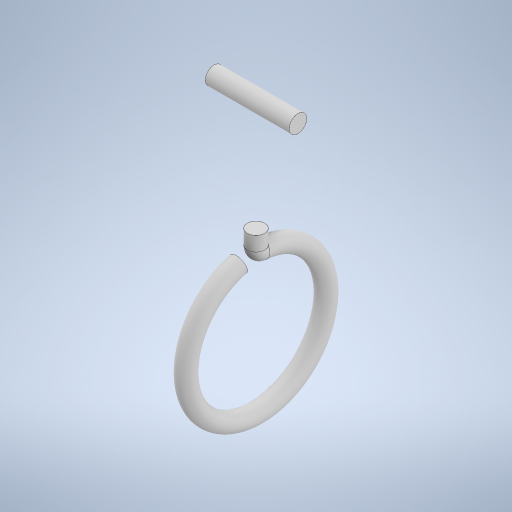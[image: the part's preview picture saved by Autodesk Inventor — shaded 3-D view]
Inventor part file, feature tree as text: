
AUTODESK INVENTOR PART (.ipt)
format: ipt  version: 2023 (Build 270158000, 158)  size: 293,376 bytes
history: native  units: in
note: dims shown in document units (in); Inventor stores cm internally (conversion verified against a paired STEP export)
features: sketch x3, sweep x1, revolve x1
ambient origin geometry x8: Origin, YZ Plane, XZ Plane, XY Plane, X Axis, Y Axis, Z Axis, Center Point
bodies: Body1 (feature_tree)
feature tree (5):
  sketch  "Sketch1"  dims[d0=0.25in d5=0.01in]
  sketch  "Sketch4"  dims[d7=0.0312in d8=0.125in]
  sweep  "Sweep2"
  revolve  "Revolution1"  [1 undecoded]
  sketch  "Sketch10"  dims[d16=0.0in d17=0.0in d25=0.36in d26=0.075in d27=0.15in d28=0.15in d29=0.0156in d30=90.0deg]
note: 1 required parameter value undecoded (feature->parameter linkage not recoverable at this tier; creation-order binding heuristic only, values carry confidence <= 0.55)
